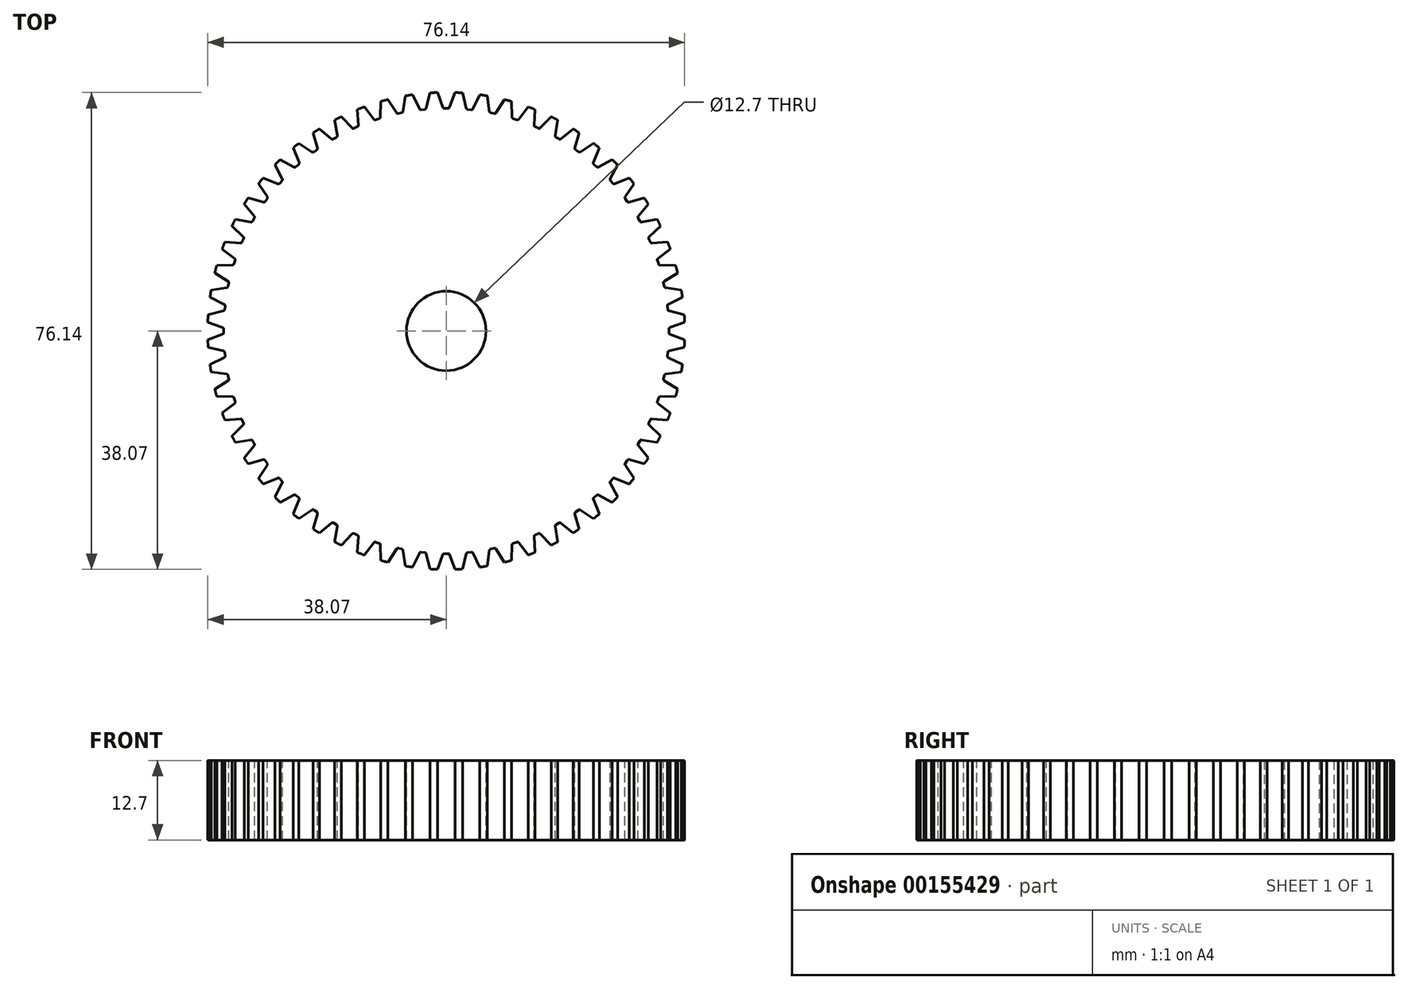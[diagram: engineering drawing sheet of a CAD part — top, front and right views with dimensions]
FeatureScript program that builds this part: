
annotation { "Feature Type Name" : "Feature", "Feature Type Description" : "" }
export const myFeature = defineFeature(function(context is Context, id is Id, definition is map)
    precondition{}
    {
        {
            var Q0;
            Q0=qCreatedBy(makeId("Top.planeOp"),FACE);
            var sketch = newSketch(context, id + "F0", { "sketchPlane" : qUnion([Q0])});
            skCircle(sketch, "E0", {"center": v(0, 0) * mm, "radius": 38.1 * mm});
            skSolve(sketch);
        }
        {
            var Q0;
            Q0=makeQuery(id+"F0.imprint","IMPRINT",FACE,{"disambiguationData":[TD([[makeQuery(id+"F0.imprint","IMPRINT",EDGE,{"derivedFrom":sQuery(id+"F0.wireOp",EDGE,"E0")}),1.0]])]});
            extrude(context, id + "F1", {"entities" : qUnion([Q0]), "depth" : 12.7 * mm});
        }
        {
            var Q0;
            Q0=makeQuery(id+"F1.opExtrude","CAP_FACE",FACE,{"disambiguationData":[OSD([sQuery(id+"F0.wireOp",EDGE,"E0")])],"isStart":false});
            var sketch = newSketch(context, id + "F2", { "sketchPlane" : qUnion([Q0])});
            skLineSegment(sketch, "E1", {"start": v(0, 0) * mm, "end": v(0, 38.1) * mm, "construction": true});
            skLineSegment(sketch, "E2", {"start": v(1.4, 38.07) * mm, "end": v(0.48, 35.54) * mm});
            skLineSegment(sketch, "E3.MirrorCS", {"start": v(-1.4, 38.07) * mm, "end": v(-0.48, 35.54) * mm});
            skLineSegment(sketch, "E4", {"start": v(-0.48, 35.54) * mm, "end": v(0.48, 35.54) * mm});
            skSolve(sketch);
        }
        {
            var Q0;
            {var subQ0=sQuery(id+"F2.wireOp",EDGE,"E2");Q0=makeQuery(id+"F2.imprint","IMPRINT",FACE,{"disambiguationData":[TD([[makeQuery(id+"F2.imprint","IMPRINT",EDGE,{"derivedFrom":subQ0}),-1.0]])]});}
            extrude(context, id + "F3", {"entities" : qUnion([Q0]), "operationType" : NewBodyOperationType.REMOVE, "oppositeDirection" : true, "depth" : 25.4 * mm});
        }
        {
            var Q0;
            Q0=makeQuery(id+"F3.boolean.opBoolean","COPY",EDGE,{"derivedFrom":makeQuery(id+"F3.opExtrude","SWEPT_EDGE",EDGE,{"disambiguationData":[OSD([sQuery(id+"F2.wireOp",EDGE,"E3.MirrorCS"),sQuery(id+"F2.wireOp",EDGE,"E4")])]})});
            var Q1;
            Q1=makeQuery(id+"F3.boolean.opBoolean","COPY",EDGE,{"derivedFrom":makeQuery(id+"F3.opExtrude","SWEPT_EDGE",EDGE,{"disambiguationData":[OSD([sQuery(id+"F2.wireOp",EDGE,"E2"),sQuery(id+"F2.wireOp",EDGE,"E4")])]})});
            fillet(context, id + "F4", {"entities" : qUnion([Q0, Q1]), "radius" : 0.25 * mm, "tangentPropagation" : true, "allowEdgeOverflow" : false});
        }
        {
            var Q0;
            Q0=makeQuery(id+"F3.boolean.opBoolean","COPY",FACE,{"derivedFrom":makeQuery(id+"F3.opExtrude","SWEPT_FACE",FACE,{"disambiguationData":[OSD([sQuery(id+"F2.wireOp",EDGE,"E3.MirrorCS")])]})});
            var Q1;
            Q1=makeQuery(id+"F4.opFillet","BLEND_FACE",FACE,{"disambiguationData":[OSD([sQuery(id+"F2.wireOp",EDGE,"E3.MirrorCS"),sQuery(id+"F2.wireOp",EDGE,"E4")])]});
            var Q2;
            Q2=makeQuery(id+"F3.boolean.opBoolean","COPY",FACE,{"derivedFrom":makeQuery(id+"F3.opExtrude","SWEPT_FACE",FACE,{"disambiguationData":[OSD([sQuery(id+"F2.wireOp",EDGE,"E4")])]})});
            var Q3;
            Q3=makeQuery(id+"F4.opFillet","BLEND_FACE",FACE,{"disambiguationData":[OSD([sQuery(id+"F2.wireOp",EDGE,"E2"),sQuery(id+"F2.wireOp",EDGE,"E4")])]});
            var Q4;
            Q4=makeQuery(id+"F3.boolean.opBoolean","COPY",FACE,{"derivedFrom":makeQuery(id+"F3.opExtrude","SWEPT_FACE",FACE,{"disambiguationData":[OSD([sQuery(id+"F2.wireOp",EDGE,"E2")])]})});
            var Q5;
            Q5=makeQuery(id+"F1.opExtrude","SWEPT_FACE",FACE,{"disambiguationData":[OSD([sQuery(id+"F0.wireOp",EDGE,"E0")])]});
            circularPattern(context, id + "F5", {"patternType" : PatternType.FACE, "faces" : qUnion([Q0, Q1, Q2, Q3, Q4]), "axis" : qUnion([Q5]), "angle" : 6 * degree, "instanceCount" : 60});
        }
        {
            var Q0;
            Q0=makeQuery(id+"F1.opExtrude","CAP_FACE",FACE,{"disambiguationData":[OSD([sQuery(id+"F0.wireOp",EDGE,"E0")])],"isStart":false});
            var sketch = newSketch(context, id + "F6", { "sketchPlane" : qUnion([Q0])});
            skCircle(sketch, "E5", {"center": v(0, 0) * mm, "radius": 6.35 * mm});
            skSolve(sketch);
        }
        {
            var Q0;
            Q0=sQuery(id+"F6.wireOp",VERTEX,"E5.center");
            var Q1;
            Q1=makeQuery(id+"F1.opExtrude","SWEPT_BODY",BODY,{"disambiguationData":[OSD([sQuery(id+"F0.wireOp",EDGE,"E0")])]});
            hole(context, id + "F7", {"style" : HoleStyle.SIMPLE, "endStyle" : HoleEndStyle.BLIND, "holeDiameter" : 12.7 * mm, "holeDepth" : 25.4 * mm, "locations" : qUnion([Q0]), "scope" : qUnion([Q1])});
        }
    });
